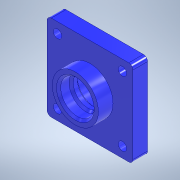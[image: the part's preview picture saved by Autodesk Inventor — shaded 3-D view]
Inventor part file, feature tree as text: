
AUTODESK INVENTOR PART (.ipt)
format: ipt  version: 2022 (Build 260153000, 153)  size: 166,400 bytes
history: native  units: mm
features: sketch x4, extrude x4, chamfer x2, projected_geometry x2, hole x1, plane x1, fillet x1
ambient origin geometry x8: Origin, YZ Plane, XZ Plane, XY Plane, X Axis, Y Axis, Z Axis, Center Point
bodies: Solid1 (feature_tree)
feature tree (15):
  sketch  "Sketch1"  dims[d0=31.0mm d1=5.0mm]
  extrude  "Extrusion1"  Depth=5.0mm
  hole  "Hole1"  [1 undecoded]
  extrude  "Extrusion2"  Depth=7.0mm TaperAngle=0.0deg
  extrude  "Extrusion3"  Depth=2.0mm
  plane  "Work Plane1"
  extrude  "Extrusion4"  TaperAngle=0.0deg  [1 undecoded]
  chamfer  "Chamfer1"  Distance=1.0mm
  fillet  "Fillet1"  Radius=4.0mm
  chamfer  "Chamfer2"  Distance=2.0mm Angle=45.0deg
  sketch  "Sketch2"  dims[d2=7.0mm d3=0.0mm]
  sketch  "Sketch3"  dims[d4=4.0mm d5=6.0mm d6=4.0mm d7=2.0mm d8=90.0deg d9=10.0mm d10=0.0mm d11=22.0mm]
  projected_geometry  "Projected Loop1"
  sketch  "Sketch4"  dims[d12=16.0mm d13=7.0mm d14=0.0mm d15=16.0mm d16=0.0mm d17=0.0mm d18=1.0mm d19=4.0mm d20=0.0mm d21=1.0mm d22=2.0mm d23=45.0deg d24=2.0mm d25=1.0mm d26=2.0mm d27=45.0deg]
  projected_geometry  "Projected Loop2"
note: 2 required parameter values undecoded (feature->parameter linkage not recoverable at this tier; creation-order binding heuristic only, values carry confidence <= 0.55)
